# Revit family: xxxDeck_Plate-American_Standard-Selectronic-Clean_IR-7020XP0_Series
name_source: partatom
category: Plumbing Fixtures
units: mm (PartAtom-declared; Revit-internal decimal feet)

## family parameters
Always vertical = No
Cut with Voids When Loaded = No
OmniClass Number = 23.45.55.14
OmniClass Title = Single Faucets
Part Type = Normal
Room Calculation Point = No
Round Connector Dimension = Use Diameter
Shared = Yes
Work Plane-Based = Yes

## types (4) — shared parameters
Assembly Code = D2020300
CW Connection = No
Default Elevation = 0"
HW Connection = No
Installation Type = Deck Mounted
Manufacturer = American Standard
Overall Length = 2 1/2"
Price = Prices may vary. Please consult Manufacturer Representative for most up-to-date price list.
Product Page URL = https://www.americanstandard-us.com
Putty Plate Included = Yes
Type Comments = Metal deck plate for use with single post Clean-IR™
Sensor faucets.
URL = http://www.americanstandard-us.com
Vent Connection = No
Warranty Information = 5 Year Limited Warranty
Waste Connection = No
zero-valued in all types: CWFU, HWFU, WFU

## per-type parameters (varying)
| type | 4" Deck Plate | 8" Deck Plate | Description | Finish | Height | Material | Overall Width | Plate Width | Putty Plate Length |
| 70204P0.002 | Yes | No | Selectronic Clean IR™ 4-Inch Deck Plate | Stainless Steel-American Standard-002-Polished Chrome | 1/4" | Stainless Steel-American Standard-002-Polished Chrome | 6 1/2" | 6 1/2" | 2 7/16" |
| 70204P0.295 | Yes | No | Selectronic Clean IR™ 4-Inch Deck Plate | Stainless Steel-American Standard-295-Brushed Nickel | 1/4" | Stainless Steel-American Standard-295-Brushed Nickel | 6 1/2" | 6 1/2" | 2 7/16" |
| 70208P0.002 | No | Yes | Selectronic Clean IR™ 8-Inch Deck Plate | Stainless Steel-American Standard-002-Polished Chrome | 3/16" | Stainless Steel-American Standard-002-Polished Chrome | 10 1/16" | 10" | 2 3/8" |
| 70208P0.295 | No | Yes | Selectronic Clean IR™ 8-Inch Deck Plate | Stainless Steel-American Standard-295-Brushed Nickel | 3/16" | Stainless Steel-American Standard-295-Brushed Nickel | 10 1/16" | 10" | 2 3/8" |

note: column(s) folded — value = type name in every type: Model

## geometry (parser evidence)
native form markers: Sweep x2
no freeform markers — native parametric forms only
